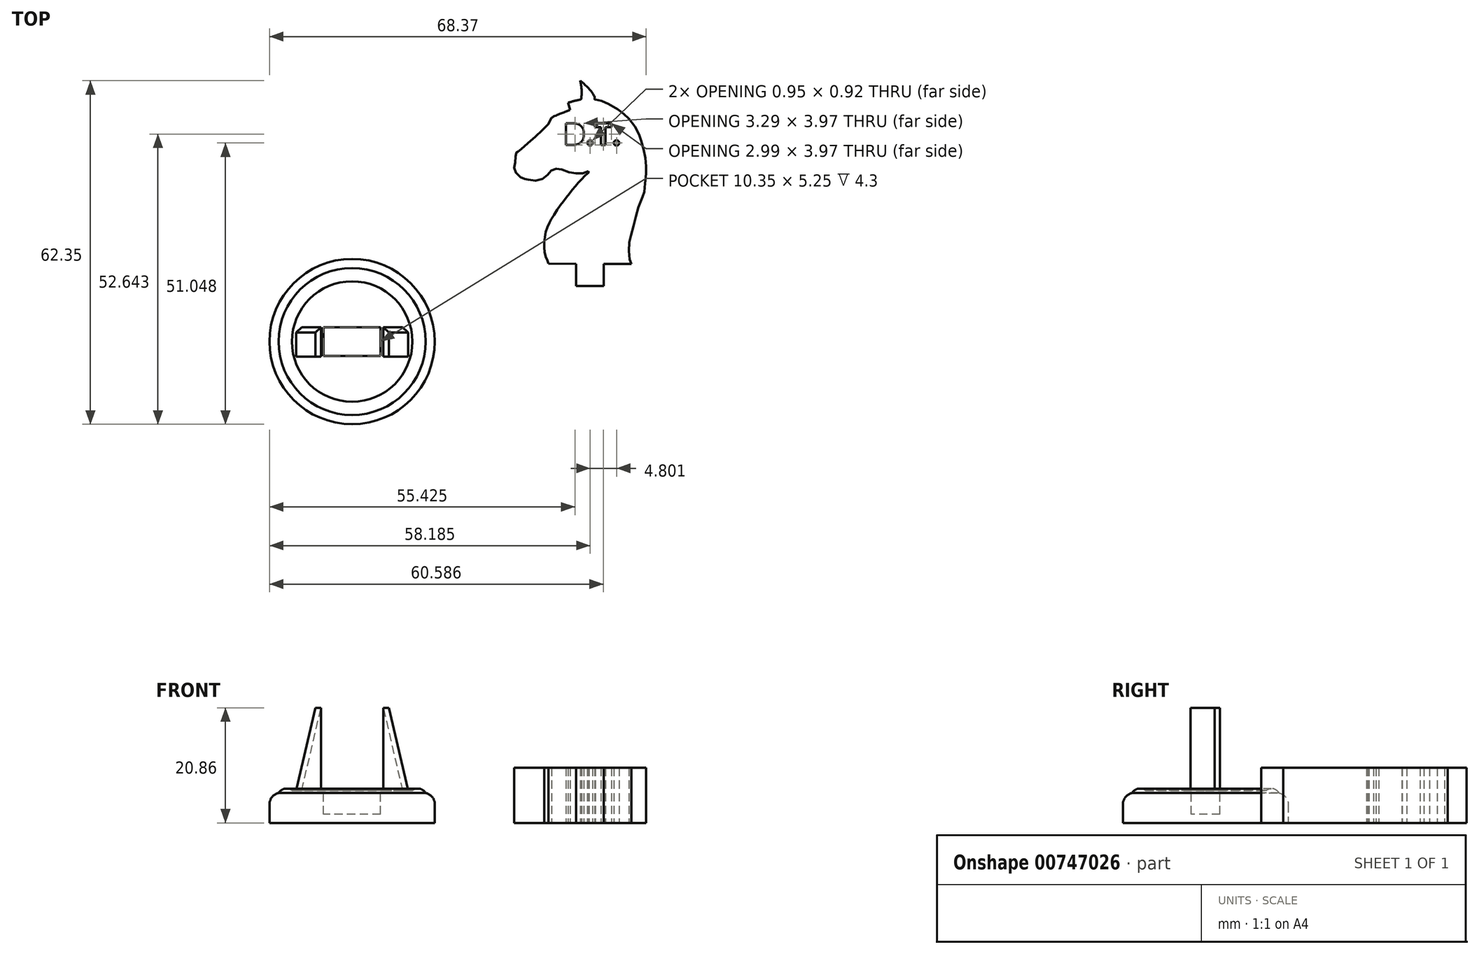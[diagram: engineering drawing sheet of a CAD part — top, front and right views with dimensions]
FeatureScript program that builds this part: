
annotation { "Feature Type Name" : "Feature", "Feature Type Description" : "" }
export const myFeature = defineFeature(function(context is Context, id is Id, definition is map)
    precondition{}
    {
        {
            var Q0;
            Q0=qCreatedBy(makeId("Top.planeOp"),FACE);
            var sketch = newSketch(context, id + "F0", { "sketchPlane" : qUnion([Q0])});
            skFitSpline(sketch, "E0", {"points": [v(35.66, 14.12) * mm, v(50.66, 14.1) * mm], "startDerivative": vector(15, -0.01) * mm, "endDerivative": vector(15, -0.01) * mm});
            skFitSpline(sketch, "E1", {"points": [v(50.66, 14.1) * mm, v(50.44, 14.55) * mm, v(50.31, 15.13) * mm, v(50.22, 17.19) * mm, v(50.4, 18.5) * mm, v(50.77, 19.83) * mm, v(51.35, 22.13) * mm, v(51.86, 24.05) * mm, v(52.76, 26.45) * mm, v(52.94, 26.92) * mm, v(53.12, 28.06) * mm, v(53.3, 30.35) * mm, v(53.37, 31.53) * mm, v(53.22, 33.08) * mm, v(52.9, 34.7) * mm, v(52.43, 36.52) * mm, v(52.1, 37.42) * mm, v(51.33, 39.05) * mm, v(50.06, 40.61) * mm, v(49.25, 41.35) * mm, v(48.08, 42.24) * mm, v(46.08, 43.38) * mm, v(45.09, 43.76) * mm, v(44.17, 43.96) * mm], "startDerivative": vector(-9.82, 17.27) * mm, "endDerivative": vector(-26.79, 4.99) * mm});
            skFitSpline(sketch, "E2", {"points": [v(44.17, 43.96) * mm, v(44, 43.96) * mm, v(44, 44.26) * mm, v(43.65, 45.03) * mm, v(43.03, 45.84) * mm, v(42.1, 46.77) * mm, v(41.38, 47.35) * mm], "startDerivative": vector(-2.58, -0.56) * mm, "endDerivative": vector(-3.55, 2.77) * mm});
            skFitSpline(sketch, "E3", {"points": [v(41.38, 47.35) * mm, v(41.51, 46.74) * mm, v(41.6, 46.13) * mm, v(41.65, 45.05) * mm, v(41.62, 44.53) * mm, v(41.56, 43.96) * mm, v(41.43, 43.92) * mm], "startDerivative": vector(0.74, -3.55) * mm, "endDerivative": vector(-1.65, -1.23) * mm});
            skFitSpline(sketch, "E4", {"points": [v(41.43, 43.92) * mm, v(40.41, 43.69) * mm, v(39.18, 43.35) * mm, v(39.17, 43.34) * mm], "startDerivative": vector(-1.88, -0.4) * mm, "endDerivative": vector(-0.04, -0.1) * mm});
            skLineSegment(sketch, "E5", {"start": v(39.18, 43.35) * mm, "end": v(39.56, 42.05) * mm});
            skFitSpline(sketch, "E6", {"points": [v(39.56, 42.05) * mm, v(39.07, 41.86) * mm, v(37.65, 41.32) * mm, v(36.2, 40.64) * mm, v(36.2, 40.63) * mm], "startDerivative": vector(-2.04, -0.8) * mm, "endDerivative": vector(0.15, -0.27) * mm});
            skFitSpline(sketch, "E7", {"points": [v(36.2, 40.64) * mm, v(35.76, 39.7) * mm, v(34.96, 38.77) * mm, v(33.93, 37.81) * mm, v(32.68, 36.66) * mm, v(31.34, 35.5) * mm, v(30.38, 34.72) * mm, v(29.81, 34.3) * mm, v(29.7, 34.09) * mm, v(29.7, 33.85) * mm, v(29.69, 33.54) * mm, v(29.64, 32.82) * mm, v(29.54, 32.36) * mm, v(29.4, 31.8) * mm, v(29.4, 31.31) * mm, v(29.62, 30.8) * mm, v(30.05, 30.28) * mm, v(30.64, 29.75) * mm, v(30.93, 29.53) * mm, v(31.3, 29.49) * mm, v(31.32, 29.62) * mm, v(31.48, 29.53) * mm, v(32.33, 29.32) * mm, v(33.27, 29.17) * mm, v(34.28, 29.41) * mm, v(35.03, 29.8) * mm, v(35.58, 30.41) * mm, v(35.89, 30.86) * mm, v(36.3, 31.17) * mm, v(36.86, 31.3) * mm, v(37.26, 31.43) * mm, v(37.86, 31.28) * mm, v(38.81, 30.88) * mm, v(39.88, 30.63) * mm, v(40.73, 30.52) * mm, v(41.54, 30.52) * mm, v(42.24, 30.66) * mm, v(42.88, 30.89) * mm], "startDerivative": vector(-11.13, -28.92) * mm, "endDerivative": vector(23.71, 9.1) * mm});
            skFitSpline(sketch, "E8", {"points": [v(42.88, 30.89) * mm, v(42.95, 30.89) * mm, v(42.98, 30.78) * mm, v(42.43, 30.27) * mm, v(41.4, 29.2) * mm, v(40.75, 28.5) * mm, v(40.08, 27.69) * mm, v(39.34, 26.76) * mm, v(38.6, 25.82) * mm, v(37.89, 24.9) * mm, v(36.97, 23.54) * mm, v(36.2, 22.27) * mm, v(35.81, 21.61) * mm, v(35.3, 20.32) * mm, v(35, 19.19) * mm, v(34.85, 17.67) * mm, v(34.9, 16.57) * mm, v(35.1, 15.54) * mm, v(35.45, 14.65) * mm, v(35.66, 14.12) * mm], "startDerivative": vector(5.2, 1.26) * mm, "endDerivative": vector(4.67, -12.25) * mm});
            skLineSegment(sketch, "E9.top", {"start": v(40.66, 10.12) * mm, "end": v(45.66, 10.12) * mm});
            skLineSegment(sketch, "E9.left", {"start": v(40.66, 14.12) * mm, "end": v(40.66, 10.12) * mm});
            skLineSegment(sketch, "E9.right", {"start": v(45.66, 14.12) * mm, "end": v(45.66, 10.12) * mm});
            skText(sketch, "E10", { "text": "D.T.", "fontName": "OpenSans-Bold.ttf"});
            const initialGuessF0  = {"E10": [0.03828, 0.03566, 1, 0, 0.004]};
            skSetInitialGuess(sketch, initialGuessF0);
            skSolve(sketch);
        }
        {
            var Q0;
            Q0=makeQuery(id+"F0.imprint","IMPRINT",FACE,{"disambiguationData":[TD([[makeQuery(id+"F0.imprint","IMPRINT",EDGE,{"derivedFrom":sQuery(id+"F0.wireOp",EDGE,"E0")}),1.0]])]});
            var Q1;
            {var subQ4=sQuery(id+"F0.wireOp",EDGE,"E9.top");Q1=makeQuery(id+"F0.imprint","IMPRINT",FACE,{"disambiguationData":[TD([[makeQuery(id+"F0.imprint","IMPRINT",EDGE,{"derivedFrom":subQ4}),1.0]])]});}
            extrude(context, id + "F1", {"entities" : qUnion([Q0, Q1]), "depth" : 10 * mm, "offsetDistance" : 25 * mm});
        }
        {
            var Q0;
            Q0=qCreatedBy(makeId("Front.planeOp"),FACE);
            var sketch = newSketch(context, id + "F2", { "sketchPlane" : qUnion([Q0])});
            skLineSegment(sketch, "E11.bottom", {"start": v(0, 0) * mm, "end": v(15, 0) * mm});
            skLineSegment(sketch, "E11.left", {"start": v(0, 0) * mm, "end": v(0, 5.86) * mm});
            skLineSegment(sketch, "E12.bottom", {"start": v(15, 0) * mm, "end": v(10.93, 0) * mm});
            skLineSegment(sketch, "E12.left", {"start": v(15, 0) * mm, "end": v(15, 3.4) * mm});
            skArc(sketch, "E13", {"start": v(15, 3.4) * mm, "mid": v(14.53, 4.7) * mm, "end": v(13.34, 5.41) * mm});
            skArc(sketch, "E14", {"start": v(13.34, 5.41) * mm, "mid": v(10.93, 5.86) * mm, "end": v(10.93, 3.4) * mm});
            skLineSegment(sketch, "E15", {"start": v(10.93, 5.86) * mm, "end": v(0, 5.86) * mm});
            skSolve(sketch);
        }
        {
            var Q0;
            Q0 = qSketchRegion(id + "F2", true);
            var Q1;
            Q1=sQuery(id+"F2.wireOp",EDGE,"E11.left");
            revolve(context, id + "F3", {"surfaceOperationType" : NewSurfaceOperationType.NEW, "entities" : qUnion([Q0]), "axis" : qUnion([Q1]), "revolveType" : RevolveType.FULL});
        }
        {
            var Q0;
            Q0=makeQuery(id+"F3.opRevolve","SWEPT_FACE",FACE,{"disambiguationData":[OSD([sQuery(id+"F2.wireOp",EDGE,"E15")])]});
            var sketch = newSketch(context, id + "F4", { "sketchPlane" : qUnion([Q0])});
            skSolve(sketch);
        }
        {
            var Q0;
            Q0=makeQuery(id+"F4.imprint","IMPRINT",FACE,{"disambiguationData":[TD([[makeQuery(id+"F4.imprint","IMPRINT",EDGE,{"derivedFrom":makeQuery(id+"F3.opRevolve","SWEPT_EDGE",EDGE,{"disambiguationData":[OSD([sQuery(id+"F2.wireOp",EDGE,"E14"),sQuery(id+"F2.wireOp",EDGE,"E15")])]})}),-1.0]])]});
            var sketch = newSketch(context, id + "F5", { "sketchPlane" : qUnion([Q0])});
            skLineSegment(sketch, "E16.bottom", {"start": v(5.17, 2.63) * mm, "end": v(-5.18, 2.63) * mm});
            skLineSegment(sketch, "E16.top", {"start": v(5.17, -2.63) * mm, "end": v(-5.18, -2.63) * mm});
            skLineSegment(sketch, "E16.left", {"start": v(5.17, 2.63) * mm, "end": v(5.17, -2.63) * mm});
            skLineSegment(sketch, "E16.right", {"start": v(-5.17, 2.62) * mm, "end": v(-5.17, -2.63) * mm});
            skPoint(sketch, "E16.middle", {"position": v(0, 0) * mm});
            skLineSegment(sketch, "E17.left", {"start": v(-5.18, 2.62) * mm, "end": v(-5.18, -2.73) * mm});
            skLineSegment(sketch, "E18.left", {"start": v(5.17, 2.63) * mm, "end": v(5.17, -2.62) * mm});
            skLineSegment(sketch, "E19.bottom", {"start": v(-5.68, 2.62) * mm, "end": v(-10.18, 2.62) * mm});
            skLineSegment(sketch, "E19.top", {"start": v(-5.67, -2.72) * mm, "end": v(-10.18, -2.72) * mm});
            skLineSegment(sketch, "E19.left", {"start": v(-5.68, 2.62) * mm, "end": v(-5.68, -2.72) * mm});
            skLineSegment(sketch, "E19.right", {"start": v(-10.18, 2.63) * mm, "end": v(-10.18, -2.72) * mm});
            skLineSegment(sketch, "E20.bottom", {"start": v(5.67, 2.63) * mm, "end": v(10.18, 2.63) * mm});
            skLineSegment(sketch, "E20.top", {"start": v(5.67, -2.72) * mm, "end": v(10.18, -2.72) * mm});
            skLineSegment(sketch, "E20.left", {"start": v(5.67, 2.63) * mm, "end": v(5.67, -2.72) * mm});
            skLineSegment(sketch, "E20.right", {"start": v(10.18, 2.63) * mm, "end": v(10.18, -2.72) * mm});
            skSolve(sketch);
        }
        {
            var Q0;
            Q0=makeQuery(id+"F5.imprint","IMPRINT",FACE,{"disambiguationData":[TD([[makeQuery(id+"F5.imprint","IMPRINT",EDGE,{"derivedFrom":sQuery(id+"F5.wireOp",EDGE,"E16.bottom")}),1.0]])]});
            extrude(context, id + "F6", {"entities" : qUnion([Q0]), "operationType" : NewBodyOperationType.REMOVE, "oppositeDirection" : true, "depth" : 4.3 * mm, "offsetDistance" : 25 * mm});
        }
        {
            var Q0;
            Q0=makeQuery(id+"F5.imprint","IMPRINT",FACE,{"disambiguationData":[TD([[makeQuery(id+"F5.imprint","IMPRINT",EDGE,{"derivedFrom":sQuery(id+"F5.wireOp",EDGE,"E19.bottom")}),1.0]])]});
            var Q1;
            Q1=makeQuery(id+"F5.imprint","IMPRINT",FACE,{"disambiguationData":[TD([[makeQuery(id+"F5.imprint","IMPRINT",EDGE,{"derivedFrom":sQuery(id+"F5.wireOp",EDGE,"E20.bottom")}),-1.0]])]});
            extrude(context, id + "F7", {"entities" : qUnion([Q0, Q1]), "operationType" : NewBodyOperationType.ADD, "depth" : 15 * mm, "offsetDistance" : 25 * mm});
        }
        {
            var Q0;
            Q0=makeQuery(id+"F7.opExtrude","SWEPT_FACE",FACE,{"disambiguationData":[OSD([sQuery(id+"F5.wireOp",EDGE,"E19.top")])]});
            var sketch = newSketch(context, id + "F8", { "sketchPlane" : qUnion([Q0])});
            skLineSegment(sketch, "E21", {"start": v(-6.67, 20.86) * mm, "end": v(-10.18, 5.86) * mm});
            skSolve(sketch);
        }
        {
            var Q0;
            {var subQ0=sQuery(id+"F8.wireOp",EDGE,"E21");Q0=makeQuery(id+"F8.imprint","IMPRINT",FACE,{"disambiguationData":[TD([[makeQuery(id+"F8.imprint","IMPRINT",EDGE,{"derivedFrom":subQ0}),-1.0]])]});}
            extrude(context, id + "F9", {"entities" : qUnion([Q0]), "operationType" : NewBodyOperationType.REMOVE, "oppositeDirection" : true, "depth" : 6 * mm, "offsetDistance" : 25 * mm});
        }
        {
            var Q0;
            Q0=makeQuery(id+"F7.opExtrude","SWEPT_FACE",FACE,{"disambiguationData":[OSD([sQuery(id+"F5.wireOp",EDGE,"E20.top")])]});
            var sketch = newSketch(context, id + "F10", { "sketchPlane" : qUnion([Q0])});
            skLineSegment(sketch, "E22", {"start": v(6.67, 20.86) * mm, "end": v(10.18, 5.86) * mm});
            skSolve(sketch);
        }
        {
            var Q0;
            {var subQ0=sQuery(id+"F10.wireOp",EDGE,"E22");Q0=makeQuery(id+"F10.imprint","IMPRINT",FACE,{"disambiguationData":[TD([[makeQuery(id+"F10.imprint","IMPRINT",EDGE,{"derivedFrom":subQ0}),1.0]])]});}
            extrude(context, id + "F11", {"entities" : qUnion([Q0]), "operationType" : NewBodyOperationType.REMOVE, "oppositeDirection" : true, "depth" : 6 * mm, "offsetDistance" : 25 * mm});
        }
        {
            var Q0;
            Q0=makeQuery(id+"F9.boolean.opBoolean","COPY",EDGE,{"derivedFrom":makeQuery(id+"F9.opExtrude","CAP_EDGE",EDGE,{"disambiguationData":[OSD([sQuery(id+"F8.wireOp",EDGE,"E21")])],"isStart":true})});
            var Q1;
            Q1=makeQuery(id+"F9.boolean.opBoolean","INTERSECT",EDGE,{"derivedFrom":[makeQuery(id+"F7.opExtrude","SWEPT_FACE",FACE,{"disambiguationData":[OSD([sQuery(id+"F5.wireOp",EDGE,"E19.bottom")])]}),makeQuery(id+"F9.opExtrude","SWEPT_FACE",FACE,{"disambiguationData":[OSD([sQuery(id+"F8.wireOp",EDGE,"E21")])]})]});
            var Q2;
            Q2=makeQuery(id+"F9.boolean.opBoolean","COPY",EDGE,{"derivedFrom":makeQuery(id+"F9.opExtrude","SWEPT_EDGE",EDGE,{"disambiguationData":[OSD([sQuery(id+"F5.wireOp",EDGE,"E19.top"),sQuery(id+"F8.wireOp",EDGE,"E21")])]})});
            var Q3;
            Q3=makeQuery(id+"F11.boolean.opBoolean","COPY",EDGE,{"derivedFrom":makeQuery(id+"F11.opExtrude","CAP_EDGE",EDGE,{"disambiguationData":[OSD([sQuery(id+"F10.wireOp",EDGE,"E22")])],"isStart":true})});
            var Q4;
            Q4=makeQuery(id+"F11.boolean.opBoolean","INTERSECT",EDGE,{"derivedFrom":[makeQuery(id+"F7.opExtrude","SWEPT_FACE",FACE,{"disambiguationData":[OSD([sQuery(id+"F5.wireOp",EDGE,"E20.bottom")])]}),makeQuery(id+"F11.opExtrude","SWEPT_FACE",FACE,{"disambiguationData":[OSD([sQuery(id+"F10.wireOp",EDGE,"E22")])]})]});
            var Q5;
            Q5=makeQuery(id+"F11.boolean.opBoolean","COPY",EDGE,{"derivedFrom":makeQuery(id+"F11.opExtrude","SWEPT_EDGE",EDGE,{"disambiguationData":[OSD([sQuery(id+"F5.wireOp",EDGE,"E20.top"),sQuery(id+"F10.wireOp",EDGE,"E22")])]})});
            chamfer(context, id + "F12", {"entities" : qUnion([Q0, Q1, Q2, Q3, Q4, Q5]), "width" : 1 * mm, "tangentPropagation" : true});
        }
    });
